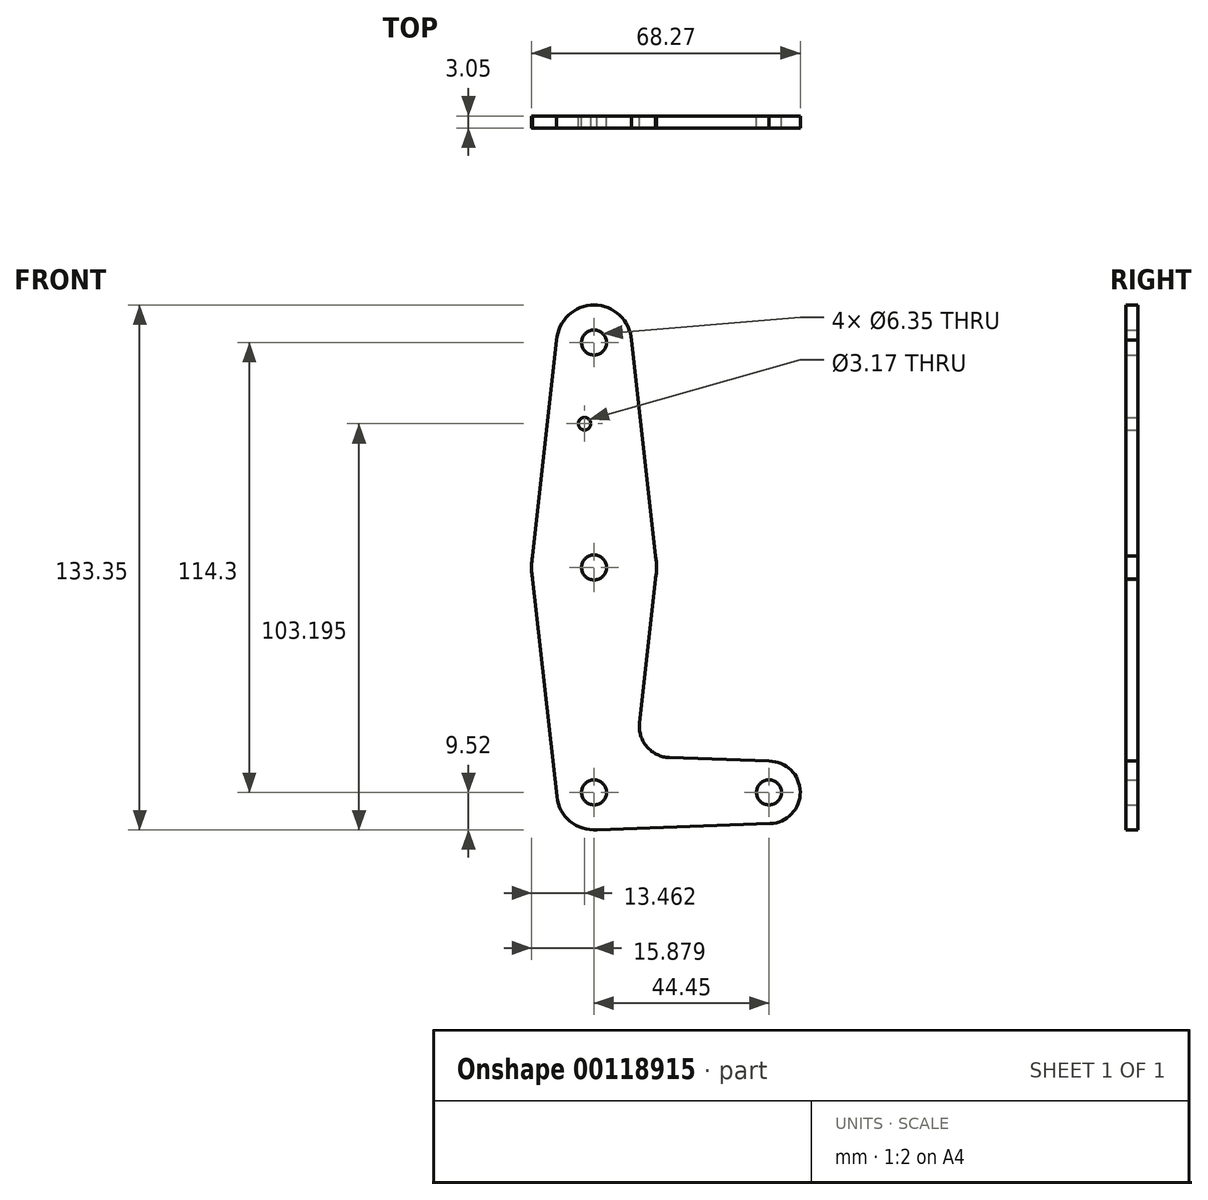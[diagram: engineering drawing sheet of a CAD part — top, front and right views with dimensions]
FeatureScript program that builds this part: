
annotation { "Feature Type Name" : "Feature", "Feature Type Description" : "" }
export const myFeature = defineFeature(function(context is Context, id is Id, definition is map)
    precondition{}
    {
        {
            var Q0;
            Q0=qCreatedBy(makeId("Front.planeOp"),FACE);
            var sketch = newSketch(context, id + "F0", { "sketchPlane" : qUnion([Q0])});
            skCircle(sketch, "E0", {"center": v(-33.7, 62.35) * mm, "radius": 9.53 * mm});
            skLineSegment(sketch, "E1", {"start": v(-33.7, 62.35) * mm, "end": v(-33.7, -51.95) * mm, "construction": true});
            skCircle(sketch, "E2", {"center": v(-33.7, 5.2) * mm, "radius": 15.88 * mm});
            skCircle(sketch, "E3", {"center": v(-33.7, -51.95) * mm, "radius": 9.53 * mm});
            skLineSegment(sketch, "E4", {"start": v(-33.7, -51.95) * mm, "end": v(10.76, -51.95) * mm, "construction": true});
            skCircle(sketch, "E5", {"center": v(10.76, -51.95) * mm, "radius": 7.94 * mm});
            skLineSegment(sketch, "E6", {"start": v(-43.2, 62.96) * mm, "end": v(-49.56, 5.73) * mm});
            skLineSegment(sketch, "E7", {"start": v(-49.56, 4.67) * mm, "end": v(-43.16, -53) * mm});
            skLineSegment(sketch, "E8", {"start": v(-24.19, 62.96) * mm, "end": v(-17.82, 5.73) * mm});
            skLineSegment(sketch, "E9", {"start": v(-17.82, 4.67) * mm, "end": v(-22.15, -34.29) * mm});
            skLineSegment(sketch, "E10", {"start": v(-14.53, -43.1) * mm, "end": v(10.76, -44.01) * mm});
            skLineSegment(sketch, "E11", {"start": v(-33.8, -61.47) * mm, "end": v(11.04, -59.88) * mm});
            skCircle(sketch, "E12", {"center": v(-33.7, 62.35) * mm, "radius": 3.18 * mm});
            skCircle(sketch, "E13", {"center": v(-36.1, 41.73) * mm, "radius": 1.59 * mm});
            skCircle(sketch, "E14", {"center": v(-33.7, 5.2) * mm, "radius": 3.18 * mm});
            skCircle(sketch, "E15", {"center": v(-33.7, -51.95) * mm, "radius": 3.18 * mm});
            skCircle(sketch, "E16", {"center": v(10.76, -51.95) * mm, "radius": 3.18 * mm});
            skPoint(sketch, "E17.newPointA", {"position": v(-24.22, -53) * mm});
            skArc(sketch, "E17.filletArc", {"start": v(-22.15, -34.29) * mm, "mid": v(-20.26, -40.36) * mm, "end": v(-14.53, -43.1) * mm});
            skSolve(sketch);
        }
        {
            var Q0;
            Q0 = qSketchRegion(id + "F0", true);
            var Q1;
            Q1 = qSketchRegion(id + "F2", true);
            extrude(context, id + "F1", {"entities" : qUnion([Q0, Q1]), "depth" : 3.05 * mm});
        }
    });
